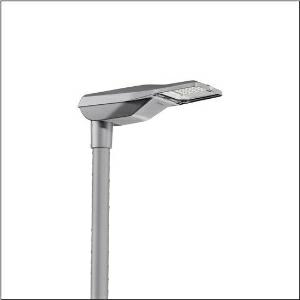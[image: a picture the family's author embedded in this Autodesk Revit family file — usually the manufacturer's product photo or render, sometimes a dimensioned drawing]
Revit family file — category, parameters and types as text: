
# Revit family: streetlight_sl_21_iq_micro___st0_8a_5xe1c31g08cb_6ed2
name_source: partatom
category: Lighting Fixtures
units: mm (PartAtom-declared; Revit-internal decimal feet)

## family parameters
Cut with Voids When Loaded = No
Host = Face
Light Source = No
Part Type = Normal
Room Calculation Point = No
Round Connector Dimension = Use Diameter
Shared = No

## types (1)
- --- (1 x LED, 2870 lm, 19.4 W, 3000K)
    Apparent Load = 19 VA
    CIE Flux Codes = 38 75 97 100 100
    Color Rendering = 70
    Color Temperature = 3000K
    Default Elevation = 1800 mm
    Description = Streetlight SL 21 iQ micro, mast luminaire, primary light control with lens, of PMMA, primary optical cover: cover, of toughened safety glass, transparent, light distribution: ST0.8a, light emission: direct distribution, primary light characteristic: asymmetric, installation type: post-top, side-entry, LED, High Power LED, rated luminous flux: 2.870lm, luminous efficacy: 148lm/W, light colour: 730, colour temperature: 3000K, control gear: iQ Street-Remote, control: Street-Remote, Auto-Match, Temp-Guard, Lumen-Switch, Night-Set, Smart-Wire, Light-Fading, Desk-Remote (wireless, voltage-free reading and setting of iQ features in the workshop via application-optimized NFC function/RFID function), optimised constant luminous flux control (CLO 2.0), pre-setting: linear dimming characteristic, mains connection: 220..240V, AC, 50/60Hz, start of lifetime: 19W, end of service life: 20W, reduction: 10W, luminaire housing, of diecast aluminium, powder-coated, Siteco® metallic grey (DB 702S), corrosivity category C5 mid according to DIN EN ISO 12944, please order mast flange separately, inclination adjustable: 0°, 5°, 10°, 15°, sealing non-destructively replaceable, multi-level sealing system, length: 528mm, width: 235mm, height: 110mm, mast flange for spigot size: 42mm (side-entry): 5XC10008XM4, 60/48mm (side-entry/post-top): 5XC10108XM2, 76/60mm (side-entry/post-top): 5XC10108XM1, protection rating (complete): IP66, insulation class (complete): insulation class II (safety insulation), certification: CE, ENEC, ENEC+, VDE, impact resistance: IK10, permissible operating ambient temperature for outdoor applications: -40..+50°C, standard-compliant lighting for roads and squares, packaging unit: 1 piece

Light Distribution: ST0.8a
    Height = 110 mm
    Lamp = 1 x LED
    Lamp Light Flux = 2870 lm
    Lamp Power = 19.4 W
    Lamp count = 1
    Length = 528 mm
    Luminous efficacy = 148 lm/W
    Manufacturer = Siteco
    ModVariant = No
    Model = 5XE1C31G08CB
    Number of Poles = 1
    OnlyDefault = Yes
    Power Factor = 1
    Product Name = Streetlight SL 21 iQ micro | ST0.8a
    Product group = mast luminaire | pylon top
    ProductGroupID = 6100
    Protection Class = Protection class II
    Protection Degree = IP 66
    RLX_Detail_Level = 1
    RLX_Emergency_Light_Flux = 0 lm
    RLX_Emergency_Type = 0
    RLX_Emergency_Type_DB = No
    RlxData = <blob elided: 98757 chars, md5=3f0b1963>
    Socket = socket
    Standby Power = 0 W
    System Light Flux = 2870 lm
    System Power = 19 W
    Type Comments = factory setting: luminous flux: 100 % | dim-lin: 254 | 387 mA
    Type Image = l_1006881.jpg
    URL = http://relux.com
    VarID = @adj_159907
    Voltage = 0 V
    Weight = 0.00 kg
    Width = 235 mm

## geometry (parser evidence)
native form markers: Blend x4, Sweep x12
no freeform markers — native parametric forms only
